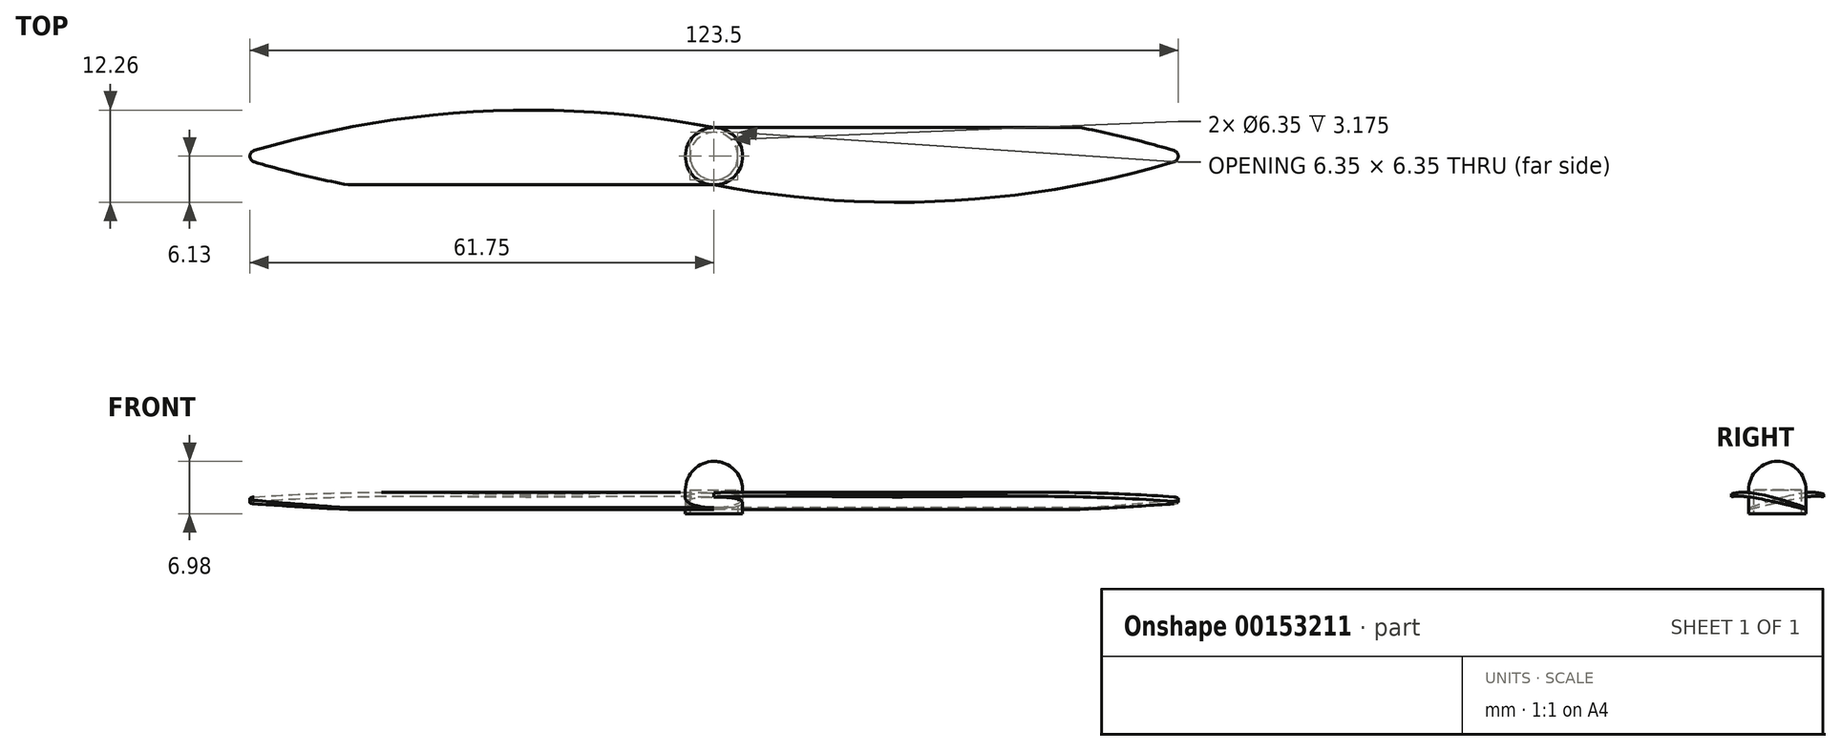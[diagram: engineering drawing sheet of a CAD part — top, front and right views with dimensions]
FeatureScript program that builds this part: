
annotation { "Feature Type Name" : "Feature", "Feature Type Description" : "" }
export const myFeature = defineFeature(function(context is Context, id is Id, definition is map)
    precondition{}
    {
        {
            var Q0;
            Q0=qCreatedBy(makeId("Top.planeOp"),FACE);
            var sketch = newSketch(context, id + "F0", { "sketchPlane" : qUnion([Q0])});
            skArc(sketch, "E0", {"start": v(0, 3.81) * mm, "mid": v(-3.81, 0) * mm, "end": v(0, -3.81) * mm});
            skArc(sketch, "E1", {"start": v(61.19, 0.75) * mm, "mid": v(30.78, 5.97) * mm, "end": v(0, 3.81) * mm});
            skArc(sketch, "E2.MirrorCS", {"start": v(61.19, -0.75) * mm, "mid": v(30.78, -5.97) * mm, "end": v(0, -3.81) * mm});
            skArc(sketch, "E3", {"start": v(61.19, -0.75) * mm, "mid": v(61.75, 0) * mm, "end": v(61.19, 0.75) * mm});
            skPoint(sketch, "E4.orphan", {"position": v(63.63, 0) * mm});
            skCircle(sketch, "E5", {"center": v(0, 0) * mm, "radius": 3.18 * mm});
            skSolve(sketch);
        }
        {
            var Q0;
            Q0=qSketchRegion(id+"F0",true);
            extrude(context, id + "F1", {"entities" : qUnion([Q0]), "depth" : 3.17 * mm});
        }
        {
            var Q0;
            Q0=qCreatedBy(makeId("Right.planeOp"),FACE);
            var sketch = newSketch(context, id + "F2", { "sketchPlane" : qUnion([Q0])});
            skLineSegment(sketch, "E6.0.0", {"start": v(-3.81, 0) * mm, "end": v(3.81, 0) * mm});
            skLineSegment(sketch, "E6.0.2", {"start": v(3.81, 3.18) * mm, "end": v(-3.81, 3.18) * mm});
            skLineSegment(sketch, "E6.0.3", {"start": v(3.81, 0.8) * mm, "end": v(3.81, 0.59) * mm});
            skLineSegment(sketch, "E7", {"start": v(6.13, 3.18) * mm, "end": v(6.13, 0) * mm});
            skLineSegment(sketch, "E8", {"start": v(-6.13, 0) * mm, "end": v(-6.13, 3.18) * mm});
            skPoint(sketch, "E9.3.internal.snap0", {"position": v(-6.13, 1.59) * mm});
            skFitSpline(sketch, "E9", {"points": [v(6.13, 0) * mm, v(-2.04, 1.94) * mm, v(-6.13, 2.25) * mm, v(-7.08, 1.59) * mm], "startDerivative": vector(-17.73, 4.52) * mm, "endDerivative": vector(-4.2, -4.46) * mm});
            skFitSpline(sketch, "E10", {"points": [v(6.13, 0) * mm, v(-2.04, 2.54) * mm, v(-6.13, 2.63) * mm, v(-8.27, 1.21) * mm], "startDerivative": vector(-19.48, 6.83) * mm, "endDerivative": vector(-7.92, -6.98) * mm});
            skLineSegment(sketch, "E11", {"start": v(6.13, 3.18) * mm, "end": v(-6.13, 3.18) * mm});
            skLineSegment(sketch, "E12", {"start": v(6.13, 0) * mm, "end": v(-6.13, 0) * mm});
            skLineSegment(sketch, "E13", {"start": v(-6.13, 2.63) * mm, "end": v(-6.13, 2.25) * mm});
            skSolve(sketch);
        }
        {
            var Q0;
            {var subQ4=sQuery(id+"F2.wireOp",EDGE,"E7");Q0=makeQuery(id+"F2.imprint","IMPRINT",FACE,{"disambiguationData":[TD([[makeQuery(id+"F2.imprint","IMPRINT",EDGE,{"derivedFrom":subQ4}),-1.0]])]});}
            var Q1;
            {var subQ0=sQuery(id+"F2.wireOp",EDGE,"E12");var subQ1=sQuery(id+"F2.wireOp",EDGE,"E8");var subQ2=makeQuery(id+"F2.imprint","INTERSECT",VERTEX,{"derivedFrom":[subQ1,subQ0]});Q1=makeQuery(id+"F2.imprint","IMPRINT",FACE,{"disambiguationData":[TD([[makeQuery(id+"F2.imprint","IMPRINT",EDGE,{"disambiguationData":[TD([[subQ2,-1.0]])],"derivedFrom":subQ1}),-1.0]])]});}
            var Q2;
            {var subQ0=sQuery(id+"F2.wireOp",EDGE,"E6.0.3");Q2=makeQuery(id+"F2.imprint","IMPRINT",FACE,{"disambiguationData":[TD([[makeQuery(id+"F2.imprint","IMPRINT",EDGE,{"derivedFrom":subQ0}),1.0]])]});}
            extrude(context, id + "F3", {"entities" : qUnion([Q0, Q1, Q2]), "operationType" : NewBodyOperationType.REMOVE, "depth" : 132.71 * mm});
        }
        {
            var Q0;
            Q0=qCreatedBy(makeId("Right.planeOp"),FACE);
            var sketch = newSketch(context, id + "F4", { "sketchPlane" : qUnion([Q0])});
            skLineSegment(sketch, "E14", {"start": v(0, 0) * mm, "end": v(0, 34.95) * mm});
            skSolve(sketch);
        }
        {
            var Q0;
            Q0=makeQuery(id+"F1.opExtrude","SWEPT_BODY",BODY,{"disambiguationData":[OSD([sQuery(id+"F0.wireOp",EDGE,"E0"),sQuery(id+"F0.wireOp",EDGE,"E1"),sQuery(id+"F0.wireOp",EDGE,"E2.MirrorCS"),sQuery(id+"F0.wireOp",EDGE,"E3"),sQuery(id+"F0.wireOp",EDGE,"E5")])]});
            var Q1;
            Q1=sQuery(id+"F4.wireOp",EDGE,"E14");
            circularPattern(context, id + "F5", {"operationType" : NewBodyOperationType.ADD, "entities" : qUnion([Q0]), "axis" : qUnion([Q1]), "angle" : 360 * degree, "instanceCount" : 2, "equalSpace" : true});
        }
        {
            var Q0;
            Q0=qCreatedBy(makeId("Front.planeOp"),FACE);
            var sketch = newSketch(context, id + "F6", { "sketchPlane" : qUnion([Q0])});
            skLineSegment(sketch, "E15", {"start": v(-3.81, 0) * mm, "end": v(-3.81, 3.18) * mm});
            skLineSegment(sketch, "E16", {"start": v(3.81, 3.18) * mm, "end": v(3.81, 0) * mm});
            skLineSegment(sketch, "E17.0", {"start": v(-3.81, 3.18) * mm, "end": v(3.81, 3.18) * mm});
            skArc(sketch, "E18", {"start": v(3.81, 3.18) * mm, "mid": v(2.7, 5.87) * mm, "end": v(0, 6.99) * mm});
            skLineSegment(sketch, "E19", {"start": v(0, 3.18) * mm, "end": v(0, 9) * mm});
            skSolve(sketch);
        }
        {
            var Q0;
            Q0=qSketchRegion(id+"F6",true);
            var Q1;
            Q1=sQuery(id+"F6.wireOp",EDGE,"E19");
            revolve(context, id + "F7", {"operationType" : NewBodyOperationType.ADD, "entities" : qUnion([Q0]), "axis" : qUnion([Q1]), "revolveType" : RevolveType.FULL});
        }
        {
            var Q0;
            Q0=makeQuery(id+"F1.opExtrude","SWEPT_BODY",BODY,{"disambiguationData":[OSD([sQuery(id+"F0.wireOp",EDGE,"E0"),sQuery(id+"F0.wireOp",EDGE,"E1"),sQuery(id+"F0.wireOp",EDGE,"E2.MirrorCS"),sQuery(id+"F0.wireOp",EDGE,"E3"),sQuery(id+"F0.wireOp",EDGE,"E5")])]});
            transform(context, id + "F8", {"entities" : qUnion([Q0]), "transformType" : TransformType.TRANSLATION_3D, "dx" : 0 * mm, "dy" : 0 * mm, "dz" : 0 * mm, "makeCopy" : true});
        }
    });
